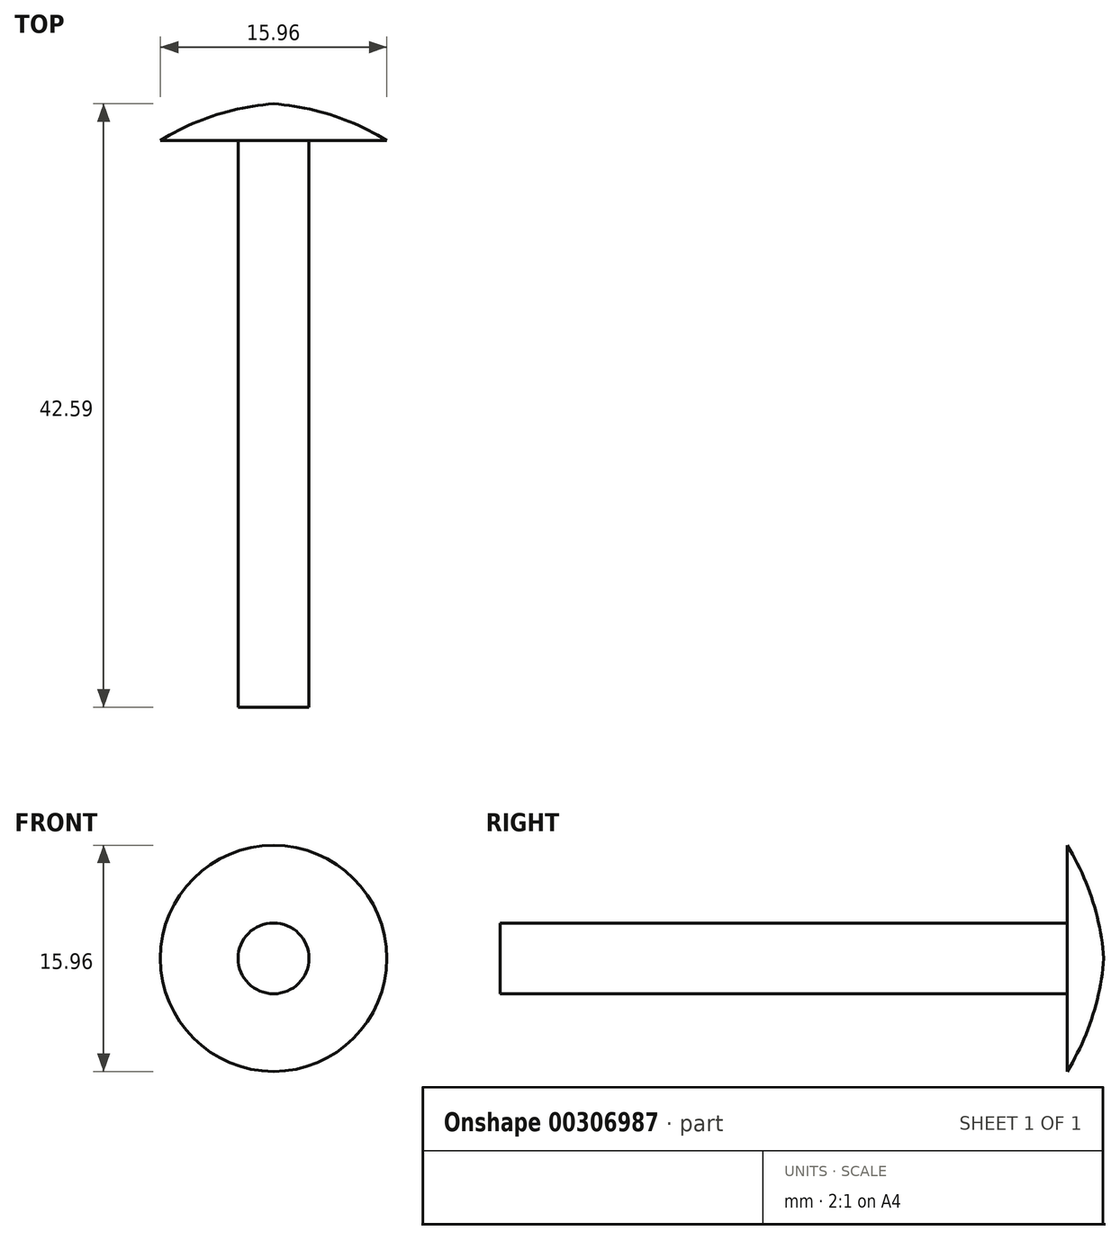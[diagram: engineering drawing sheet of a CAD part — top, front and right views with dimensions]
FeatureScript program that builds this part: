
annotation { "Feature Type Name" : "Feature", "Feature Type Description" : "" }
export const myFeature = defineFeature(function(context is Context, id is Id, definition is map)
    precondition{}
    {
        {
            var Q0;
            Q0=qCreatedBy(makeId("Top.planeOp"),FACE);
            var sketch = newSketch(context, id + "F0", { "sketchPlane" : qUnion([Q0])});
            skLineSegment(sketch, "E0", {"start": v(0, 0) * mm, "end": v(-2.5, 0) * mm});
            skLineSegment(sketch, "E1", {"start": v(-2.5, 0) * mm, "end": v(-2.5, 40) * mm});
            skLineSegment(sketch, "E2", {"start": v(-2.5, 40) * mm, "end": v(-7.98, 40) * mm});
            skLineSegment(sketch, "E3", {"start": v(0, 0) * mm, "end": v(0, 21.96) * mm, "construction": true});
            skArc(sketch, "E4", {"start": v(0, 42.6) * mm, "mid": v(-4.15, 41.78) * mm, "end": v(-7.98, 40) * mm});
            skLineSegment(sketch, "E5", {"start": v(0, 42.6) * mm, "end": v(0, 0) * mm});
            skSolve(sketch);
        }
        {
            var Q0;
            Q0=makeQuery(id+"F0.imprint","IMPRINT",FACE,{"disambiguationData":[TD([[makeQuery(id+"F0.imprint","IMPRINT",EDGE,{"derivedFrom":sQuery(id+"F0.wireOp",EDGE,"E0")}),-1.0]])]});
            var Q1;
            Q1=sQuery(id+"F0.wireOp",EDGE,"E5");
            revolve(context, id + "F1", {"entities" : qUnion([Q0]), "axis" : qUnion([Q1]), "revolveType" : RevolveType.FULL});
        }
    });
